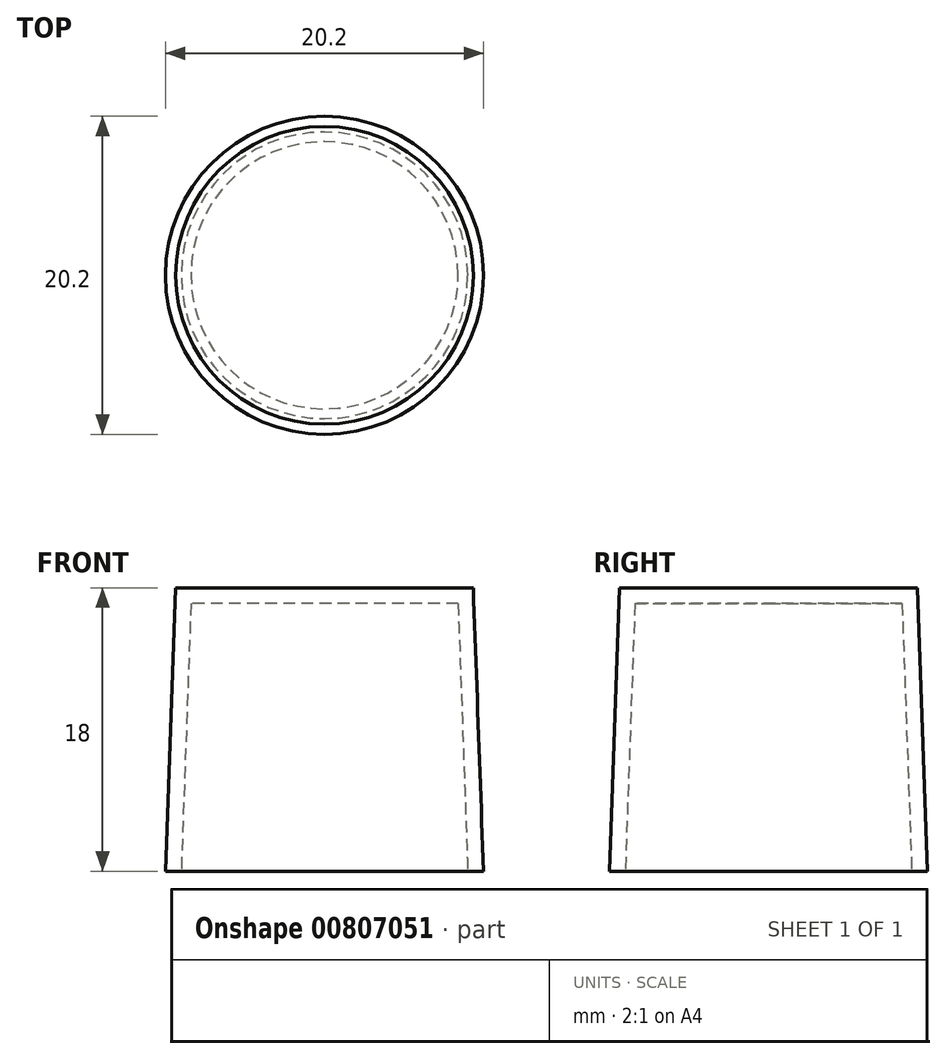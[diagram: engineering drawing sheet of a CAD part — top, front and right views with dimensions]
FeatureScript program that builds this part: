
annotation { "Feature Type Name" : "Feature", "Feature Type Description" : "" }
export const myFeature = defineFeature(function(context is Context, id is Id, definition is map)
    precondition{}
    {
        {
            assignVariable(context, id + "F0", {"name" : "wand", "anyValue" : 1});
        }
        {
            assignVariable(context, id + "F1", {"name" : "h", "anyValue" : 18});
        }
        {
            var Q0;
            Q0=qCreatedBy(makeId("Top.planeOp"),FACE);
            var sketch = newSketch(context, id + "F2", { "sketchPlane" : qUnion([Q0])});
            skCircle(sketch, "E0", {"center": v(0, 0) * mm, "radius": 9.45 * mm});
            skSolve(sketch);
        }
        {
            var Q0;
            Q0=qCreatedBy(makeId("Top.planeOp"),FACE);
            cPlane(context, id + "F3", {"entities" : qUnion([Q0]), "cplaneType" : CPlaneType.OFFSET, "offset" : (getVariable(context, 'h')) * mm, "oppositeDirection" : true, "width" : 150 * mm, "height" : 150 * mm});
        }
        {
            var Q0;
            Q0=qCreatedBy(id+"F3.planeOp",FACE);
            var sketch = newSketch(context, id + "F4", { "sketchPlane" : qUnion([Q0])});
            skCircle(sketch, "E1", {"center": v(0, 0) * mm, "radius": 10.1 * mm});
            skSolve(sketch);
        }
        {
            var Q0;
            Q0=makeQuery(id+"F2.imprint","IMPRINT",FACE,{"disambiguationData":[TD([[makeQuery(id+"F2.imprint","IMPRINT",EDGE,{"derivedFrom":sQuery(id+"F2.wireOp",EDGE,"E0")}),1.0]])]});
            var Q1;
            Q1=makeQuery(id+"F4.imprint","IMPRINT",FACE,{"disambiguationData":[TD([[makeQuery(id+"F4.imprint","IMPRINT",EDGE,{"derivedFrom":sQuery(id+"F4.wireOp",EDGE,"E1")}),1.0]])]});
            loft(context, id + "F5", {"sheetProfilesArray" : [{ "sheetProfileEntities" : qUnion([Q0]) }, { "sheetProfileEntities" : qUnion([Q1]) }]});
        }
        {
            var Q0;
            Q0=makeQuery(id+"F5.opLoft","CAP_FACE",FACE,{"disambiguationData":[OSD([makeQuery(id+"F4.imprint","IMPRINT",FACE,{"disambiguationData":[TD([[makeQuery(id+"F4.imprint","IMPRINT",EDGE,{"derivedFrom":sQuery(id+"F4.wireOp",EDGE,"E1")}),1.0]])]})])],"isStart":true});
            shell(context, id + "F6", {"entities" : qUnion([Q0]), "thickness" : (getVariable(context, 'wand')) * mm});
        }
    });
